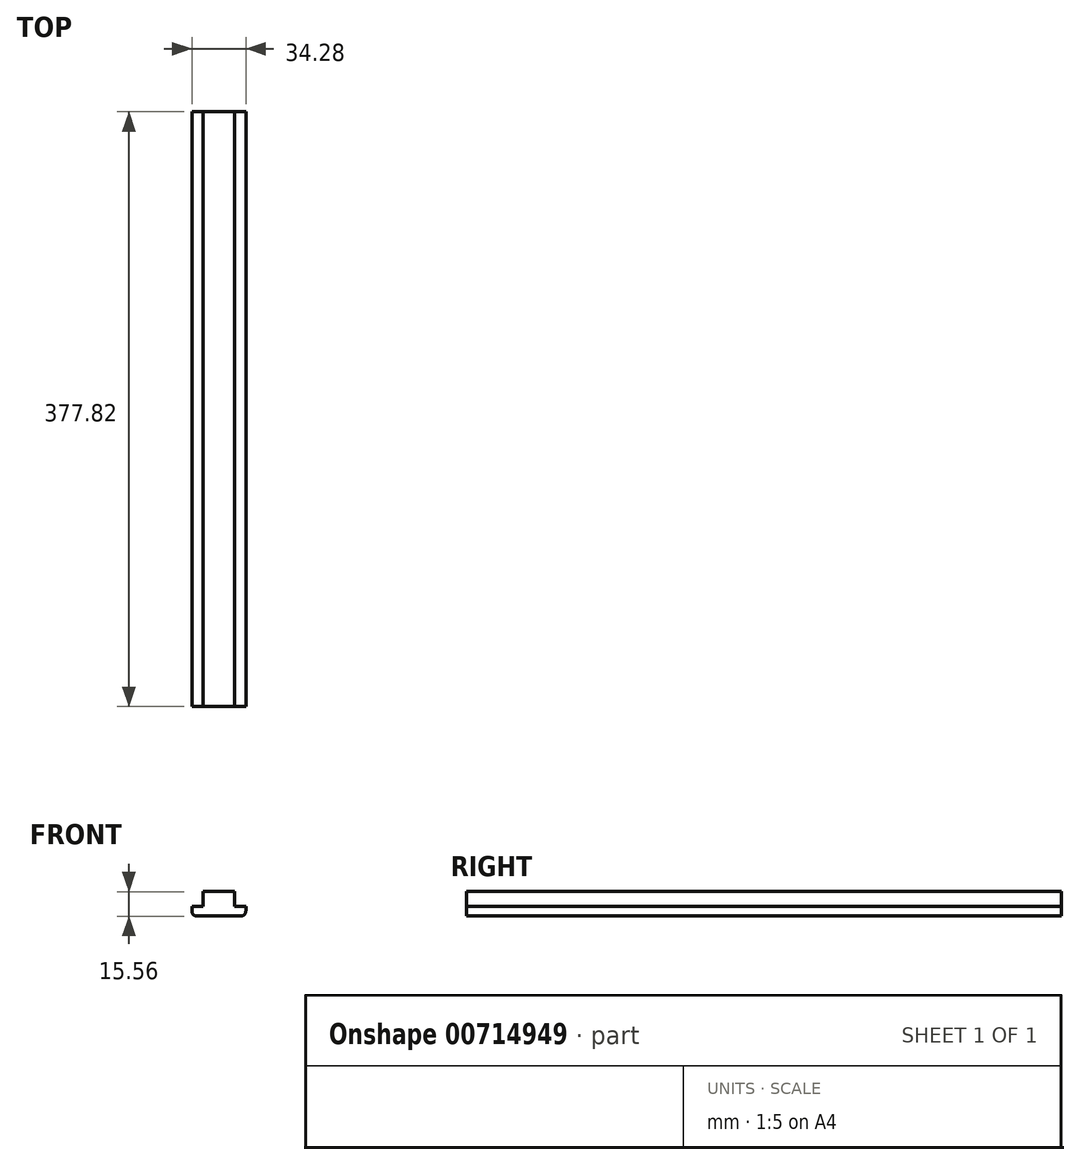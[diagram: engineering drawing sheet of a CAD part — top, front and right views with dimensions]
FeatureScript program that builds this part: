
annotation { "Feature Type Name" : "Feature", "Feature Type Description" : "" }
export const myFeature = defineFeature(function(context is Context, id is Id, definition is map)
    precondition{}
    {
        {
            var Q0;
            Q0=qCreatedBy(makeId("Front.planeOp"),FACE);
            var sketch = newSketch(context, id + "F0", { "sketchPlane" : qUnion([Q0])});
            skPoint(sketch, "E0.middle", {"position": v(0, 0) * mm});
            skPoint(sketch, "E1.visualSharp", {"position": v(-41.28, 9.53) * mm});
            skPoint(sketch, "E2.visualSharp", {"position": v(41.28, 9.53) * mm});
            skPoint(sketch, "E3.end.orphan", {"position": v(10.16, 2.89) * mm});
            skPoint(sketch, "E4.right.end.orphan", {"position": v(10.19, 0) * mm});
            skLineSegment(sketch, "E5.bottom", {"start": v(-13.97, -3.18) * mm, "end": v(13.97, -3.18) * mm});
            skLineSegment(sketch, "E5.top", {"start": v(-17.78, 2.89) * mm, "end": v(-10.16, 2.89) * mm});
            skLineSegment(sketch, "E5.left", {"start": v(-17.15, 0) * mm, "end": v(-17.15, 2.92) * mm});
            skLineSegment(sketch, "E5.right", {"start": v(17.15, 0) * mm, "end": v(17.15, 2.89) * mm});
            skLineSegment(sketch, "E6", {"start": v(-10.16, 12.38) * mm, "end": v(-10.16, 2.89) * mm});
            skLineSegment(sketch, "E7", {"start": v(10.16, 12.38) * mm, "end": v(10.16, 2.89) * mm});
            skLineSegment(sketch, "E8.trimOffspring", {"start": v(10.16, 2.89) * mm, "end": v(17.15, 2.89) * mm});
            skPoint(sketch, "E1.filletArc.center.orphan", {"position": v(-35.24, 2.89) * mm});
            skPoint(sketch, "E9.visualSharp", {"position": v(-41.28, 9.52) * mm});
            skLineSegment(sketch, "E10", {"start": v(-10.16, 12.38) * mm, "end": v(10.16, 12.38) * mm});
            skPoint(sketch, "E0.bottom.end.orphan", {"position": v(-41.28, -9.53) * mm});
            skPoint(sketch, "E0.left.start.orphan", {"position": v(41.28, -9.52) * mm});
            skPoint(sketch, "E11.visualSharp", {"position": v(-17.15, -3.18) * mm});
            skArc(sketch, "E11.filletArc", {"start": v(-17.15, 0) * mm, "mid": v(-16.22, -2.25) * mm, "end": v(-13.97, -3.17) * mm});
            skPoint(sketch, "E12.visualSharp", {"position": v(17.78, -3.18) * mm});
            skArc(sketch, "E12.filletArc", {"start": v(13.97, -3.17) * mm, "mid": v(16.22, -2.25) * mm, "end": v(17.15, 0) * mm});
            skSolve(sketch);
        }
        {
            var Q0;
            Q0=qSketchRegion(id+"F0",true);
            extrude(context, id + "F1", {"entities" : qUnion([Q0]), "endBound" : BoundingType.SYMMETRIC, "depth" : 377.82 * mm, "offsetDistance" : 25.4 * mm});
        }
    });
